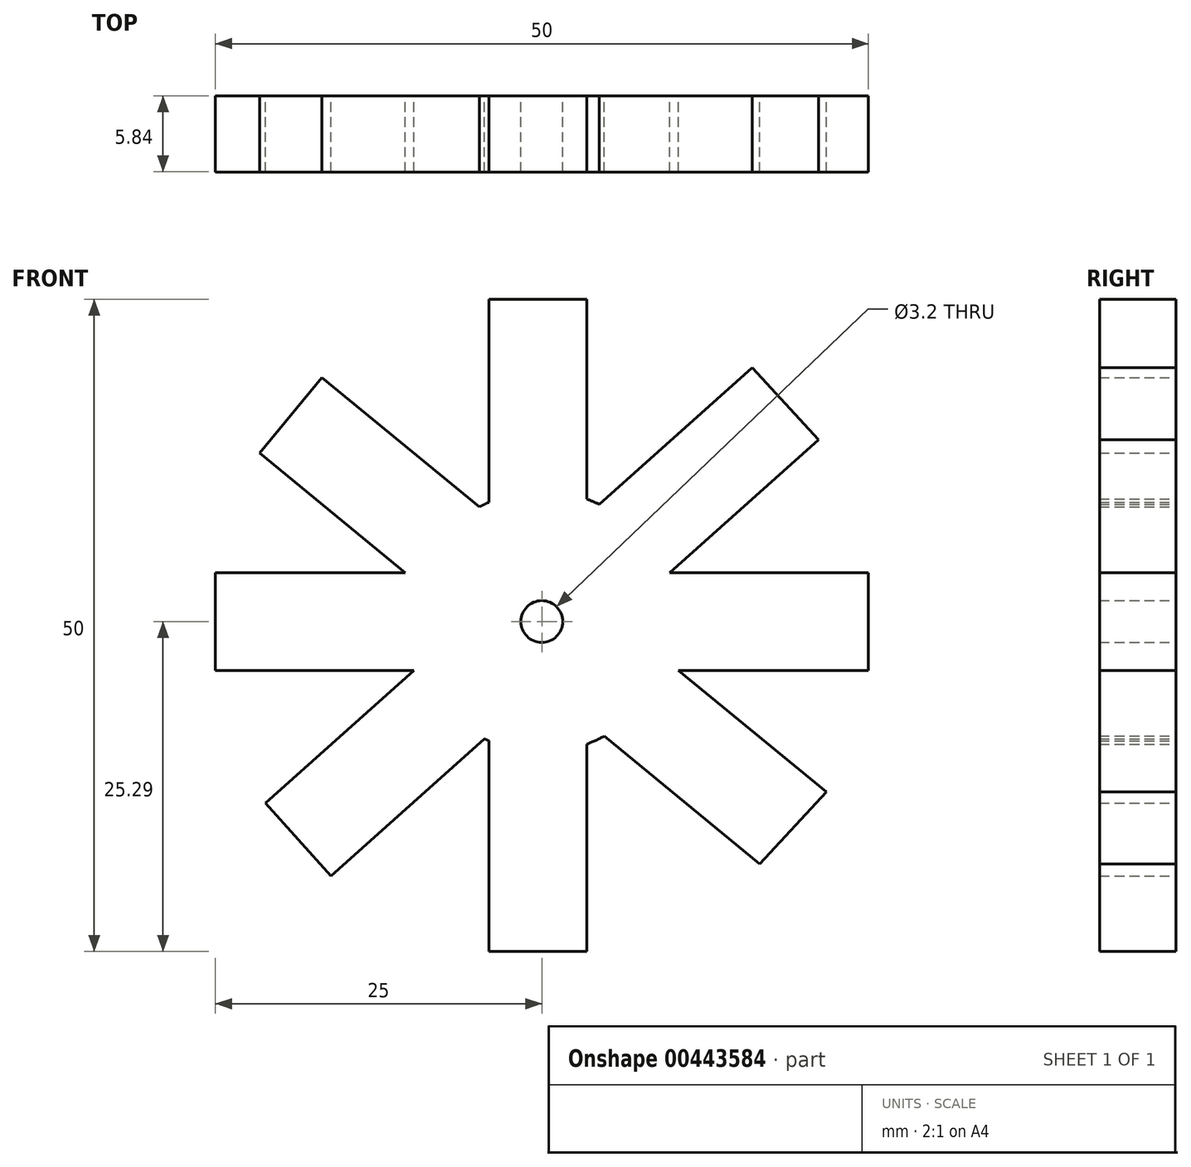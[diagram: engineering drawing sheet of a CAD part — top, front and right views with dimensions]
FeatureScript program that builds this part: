
annotation { "Feature Type Name" : "Feature", "Feature Type Description" : "" }
export const myFeature = defineFeature(function(context is Context, id is Id, definition is map)
    precondition{}
    {
        {
            var Q0;
            Q0=qCreatedBy(makeId("Front.planeOp"),FACE);
            var sketch = newSketch(context, id + "F0", { "sketchPlane" : qUnion([Q0])});
            skCircle(sketch, "E0", {"center": v(0, 0) * mm, "radius": 10 * mm});
            skCircle(sketch, "E1", {"center": v(0, 0) * mm, "radius": 1.6 * mm});
            skLineSegment(sketch, "E2.right", {"start": v(0, 2.75) * mm, "end": v(0, -2.75) * mm});
            skLineSegment(sketch, "E3.bottom", {"start": v(-4.06, 24.71) * mm, "end": v(3.44, 24.71) * mm});
            skLineSegment(sketch, "E3.top", {"start": v(-4.06, -25.29) * mm, "end": v(3.44, -25.29) * mm});
            skLineSegment(sketch, "E3.left", {"start": v(-4.06, 24.71) * mm, "end": v(-4.06, -25.29) * mm});
            skLineSegment(sketch, "E3.right", {"start": v(3.44, 24.71) * mm, "end": v(3.44, -25.29) * mm});
            skLineSegment(sketch, "E4", {"start": v(-21.15, -13.9) * mm, "end": v(16.1, 19.45) * mm});
            skLineSegment(sketch, "E5", {"start": v(-21.15, -13.9) * mm, "end": v(-16.15, -19.5) * mm});
            skLineSegment(sketch, "E6", {"start": v(-16.15, -19.5) * mm, "end": v(21.2, 13.95) * mm});
            skLineSegment(sketch, "E7", {"start": v(16.1, 19.45) * mm, "end": v(21.2, 13.95) * mm});
            skPoint(sketch, "E8", {"position": v(3.44, -0.29) * mm});
            skPoint(sketch, "E9", {"position": v(-0.31, 24.71) * mm});
            skPoint(sketch, "E10", {"position": v(-18.65, -16.7) * mm});
            skPoint(sketch, "E11", {"position": v(18.65, 16.7) * mm});
            skLineSegment(sketch, "E12.bottom", {"start": v(-25, 3.75) * mm, "end": v(25, 3.75) * mm});
            skLineSegment(sketch, "E12.top", {"start": v(-25, -3.75) * mm, "end": v(25, -3.75) * mm});
            skLineSegment(sketch, "E12.left", {"start": v(-25, 3.75) * mm, "end": v(-25, -3.75) * mm});
            skLineSegment(sketch, "E12.right", {"start": v(25, 3.75) * mm, "end": v(25, -3.75) * mm});
            skPoint(sketch, "E13", {"position": v(-25, 0) * mm});
            skPoint(sketch, "E14", {"position": v(25, 0) * mm});
            skLineSegment(sketch, "E15", {"start": v(-21.61, 12.9) * mm, "end": v(16.69, -18.56) * mm});
            skLineSegment(sketch, "E16", {"start": v(-21.61, 12.9) * mm, "end": v(-16.85, 18.7) * mm});
            skLineSegment(sketch, "E17", {"start": v(-16.85, 18.7) * mm, "end": v(21.78, -13.04) * mm});
            skLineSegment(sketch, "E18", {"start": v(16.69, -18.56) * mm, "end": v(21.78, -13.04) * mm});
            skPoint(sketch, "E19", {"position": v(-19.23, 15.8) * mm});
            skPoint(sketch, "E20", {"position": v(19.23, -15.8) * mm});
            skSolve(sketch);
        }
        {
            var Q0;
            Q0 = qSketchRegion(id + "F0", true);
            var Q1;
            {var subQ0=sQuery(id+"F0.wireOp",EDGE,"E12.bottom");var subQ1=sQuery(id+"F0.wireOp",EDGE,"E3.left");var subQ2=makeQuery(id+"F0.imprint","INTERSECT",VERTEX,{"derivedFrom":[subQ1,subQ0]});Q1=makeQuery(id+"F0.imprint","IMPRINT",FACE,{"disambiguationData":[TD([[makeQuery(id+"F0.imprint","IMPRINT",EDGE,{"disambiguationData":[TD([[subQ2,-1.0]])],"derivedFrom":subQ1}),-1.0]])]});}
            var Q2;
            {var subQ0=sQuery(id+"F0.wireOp",EDGE,"E15");var subQ1=sQuery(id+"F0.wireOp",EDGE,"E3.left");var subQ2=makeQuery(id+"F0.imprint","INTERSECT",VERTEX,{"derivedFrom":[subQ1,subQ0]});Q2=makeQuery(id+"F0.imprint","IMPRINT",FACE,{"disambiguationData":[TD([[makeQuery(id+"F0.imprint","IMPRINT",EDGE,{"disambiguationData":[TD([[subQ2,-1.0]])],"derivedFrom":subQ1}),-1.0]])]});}
            var Q3;
            {var subQ0=sQuery(id+"F0.wireOp",EDGE,"E17");var subQ1=sQuery(id+"F0.wireOp",EDGE,"E3.left");var subQ2=makeQuery(id+"F0.imprint","INTERSECT",VERTEX,{"derivedFrom":[subQ1,subQ0]});Q3=makeQuery(id+"F0.imprint","IMPRINT",FACE,{"disambiguationData":[TD([[makeQuery(id+"F0.imprint","IMPRINT",EDGE,{"disambiguationData":[TD([[subQ2,-1.0]])],"derivedFrom":subQ1}),1.0]])]});}
            var Q4;
            {var subQ0=sQuery(id+"F0.wireOp",EDGE,"E4");var subQ1=sQuery(id+"F0.wireOp",EDGE,"E3.right");var subQ2=makeQuery(id+"F0.imprint","INTERSECT",VERTEX,{"derivedFrom":[subQ1,subQ0]});Q4=makeQuery(id+"F0.imprint","IMPRINT",FACE,{"disambiguationData":[TD([[makeQuery(id+"F0.imprint","IMPRINT",EDGE,{"disambiguationData":[TD([[subQ2,-1.0]])],"derivedFrom":subQ1}),-1.0]])]});}
            var Q5;
            {var subQ0=sQuery(id+"F0.wireOp",EDGE,"E12.bottom");var subQ1=sQuery(id+"F0.wireOp",EDGE,"E4");var subQ2=makeQuery(id+"F0.imprint","INTERSECT",VERTEX,{"derivedFrom":[subQ1,subQ0]});Q5=makeQuery(id+"F0.imprint","IMPRINT",FACE,{"disambiguationData":[TD([[makeQuery(id+"F0.imprint","IMPRINT",EDGE,{"disambiguationData":[TD([[subQ2,-1.0]])],"derivedFrom":subQ1}),-1.0]])]});}
            var Q6;
            {var subQ0=sQuery(id+"F0.wireOp",EDGE,"E17");var subQ1=sQuery(id+"F0.wireOp",EDGE,"E3.right");var subQ2=makeQuery(id+"F0.imprint","INTERSECT",VERTEX,{"derivedFrom":[subQ1,subQ0]});Q6=makeQuery(id+"F0.imprint","IMPRINT",FACE,{"disambiguationData":[TD([[makeQuery(id+"F0.imprint","IMPRINT",EDGE,{"disambiguationData":[TD([[subQ2,-1.0]])],"derivedFrom":subQ1}),1.0]])]});}
            var Q7;
            {var subQ0=sQuery(id+"F0.wireOp",EDGE,"E4");var subQ1=sQuery(id+"F0.wireOp",EDGE,"E3.left");var subQ2=makeQuery(id+"F0.imprint","INTERSECT",VERTEX,{"derivedFrom":[subQ1,subQ0]});Q7=makeQuery(id+"F0.imprint","IMPRINT",FACE,{"disambiguationData":[TD([[makeQuery(id+"F0.imprint","IMPRINT",EDGE,{"disambiguationData":[TD([[subQ2,-1.0]])],"derivedFrom":subQ1}),-1.0]])]});}
            var Q8;
            {var subQ0=sQuery(id+"F0.wireOp",EDGE,"E12.top");var subQ1=sQuery(id+"F0.wireOp",EDGE,"E3.right");var subQ2=makeQuery(id+"F0.imprint","INTERSECT",VERTEX,{"derivedFrom":[subQ1,subQ0]});Q8=makeQuery(id+"F0.imprint","IMPRINT",FACE,{"disambiguationData":[TD([[makeQuery(id+"F0.imprint","IMPRINT",EDGE,{"disambiguationData":[TD([[subQ2,-1.0]])],"derivedFrom":subQ1}),-1.0]])]});}
            var Q9;
            {var subQ0=sQuery(id+"F0.wireOp",EDGE,"E15");var subQ1=sQuery(id+"F0.wireOp",EDGE,"E6");var subQ2=makeQuery(id+"F0.imprint","INTERSECT",VERTEX,{"derivedFrom":[subQ1,subQ0]});Q9=makeQuery(id+"F0.imprint","IMPRINT",FACE,{"disambiguationData":[TD([[makeQuery(id+"F0.imprint","IMPRINT",EDGE,{"disambiguationData":[TD([[subQ2,-1.0]])],"derivedFrom":subQ1}),1.0]])]});}
            var Q10;
            {var subQ0=sQuery(id+"F0.wireOp",EDGE,"E12.bottom");var subQ1=sQuery(id+"F0.wireOp",EDGE,"E3.left");var subQ2=makeQuery(id+"F0.imprint","INTERSECT",VERTEX,{"derivedFrom":[subQ1,subQ0]});Q10=makeQuery(id+"F0.imprint","IMPRINT",FACE,{"disambiguationData":[TD([[makeQuery(id+"F0.imprint","IMPRINT",EDGE,{"disambiguationData":[TD([[subQ2,-1.0]])],"derivedFrom":subQ1}),1.0]])]});}
            var Q11;
            {var subQ5=sQuery(id+"F0.wireOp",EDGE,"E2.right");var subQ6=sQuery(id+"F0.wireOp",EDGE,"E1");var subQ7=makeQuery(id+"F0.imprint","INTERSECT",VERTEX,{"disambiguationData":[OD(0.0)],"derivedFrom":[subQ6,subQ5]});Q11=makeQuery(id+"F0.imprint","IMPRINT",FACE,{"disambiguationData":[TD([[makeQuery(id+"F0.imprint","IMPRINT",EDGE,{"disambiguationData":[TD([[subQ7,-1.0]])],"derivedFrom":subQ6}),-1.0]])]});}
            var Q12;
            {var subQ0=sQuery(id+"F0.wireOp",EDGE,"E12.top");var subQ1=sQuery(id+"F0.wireOp",EDGE,"E3.left");var subQ2=makeQuery(id+"F0.imprint","INTERSECT",VERTEX,{"derivedFrom":[subQ1,subQ0]});Q12=makeQuery(id+"F0.imprint","IMPRINT",FACE,{"disambiguationData":[TD([[makeQuery(id+"F0.imprint","IMPRINT",EDGE,{"disambiguationData":[TD([[subQ2,-1.0]])],"derivedFrom":subQ1}),1.0]])]});}
            var Q13;
            {var subQ0=sQuery(id+"F0.wireOp",EDGE,"E15");var subQ1=sQuery(id+"F0.wireOp",EDGE,"E3.left");var subQ2=makeQuery(id+"F0.imprint","INTERSECT",VERTEX,{"derivedFrom":[subQ1,subQ0]});Q13=makeQuery(id+"F0.imprint","IMPRINT",FACE,{"disambiguationData":[TD([[makeQuery(id+"F0.imprint","IMPRINT",EDGE,{"disambiguationData":[TD([[subQ2,-1.0]])],"derivedFrom":subQ1}),1.0]])]});}
            var Q14;
            {var subQ0=sQuery(id+"F0.wireOp",EDGE,"E12.bottom");var subQ1=sQuery(id+"F0.wireOp",EDGE,"E3.right");var subQ2=makeQuery(id+"F0.imprint","INTERSECT",VERTEX,{"derivedFrom":[subQ1,subQ0]});Q14=makeQuery(id+"F0.imprint","IMPRINT",FACE,{"disambiguationData":[TD([[makeQuery(id+"F0.imprint","IMPRINT",EDGE,{"disambiguationData":[TD([[subQ2,-1.0]])],"derivedFrom":subQ1}),1.0]])]});}
            var Q15;
            {var subQ6=sQuery(id+"F0.wireOp",EDGE,"E2.right");var subQ8=sQuery(id+"F0.wireOp",EDGE,"E1");var subQ13=makeQuery(id+"F0.imprint","INTERSECT",VERTEX,{"disambiguationData":[OD(0.0)],"derivedFrom":[subQ8,subQ6]});Q15=makeQuery(id+"F0.imprint","IMPRINT",FACE,{"disambiguationData":[TD([[makeQuery(id+"F0.imprint","IMPRINT",EDGE,{"disambiguationData":[TD([[subQ13,1.0]])],"derivedFrom":subQ8}),-1.0]])]});}
            var Q16;
            {var subQ0=sQuery(id+"F0.wireOp",EDGE,"E6");var subQ1=sQuery(id+"F0.wireOp",EDGE,"E3.right");var subQ2=makeQuery(id+"F0.imprint","INTERSECT",VERTEX,{"derivedFrom":[subQ1,subQ0]});Q16=makeQuery(id+"F0.imprint","IMPRINT",FACE,{"disambiguationData":[TD([[makeQuery(id+"F0.imprint","IMPRINT",EDGE,{"disambiguationData":[TD([[subQ2,-1.0]])],"derivedFrom":subQ1}),-1.0]])]});}
            var Q17;
            {var subQ0=sQuery(id+"F0.wireOp",EDGE,"E12.bottom");var subQ1=sQuery(id+"F0.wireOp",EDGE,"E3.right");var subQ2=makeQuery(id+"F0.imprint","INTERSECT",VERTEX,{"derivedFrom":[subQ1,subQ0]});Q17=makeQuery(id+"F0.imprint","IMPRINT",FACE,{"disambiguationData":[TD([[makeQuery(id+"F0.imprint","IMPRINT",EDGE,{"disambiguationData":[TD([[subQ2,-1.0]])],"derivedFrom":subQ1}),-1.0]])]});}
            var Q18;
            {var subQ0=sQuery(id+"F0.wireOp",EDGE,"E6");var subQ1=sQuery(id+"F0.wireOp",EDGE,"E3.right");var subQ2=makeQuery(id+"F0.imprint","INTERSECT",VERTEX,{"derivedFrom":[subQ1,subQ0]});Q18=makeQuery(id+"F0.imprint","IMPRINT",FACE,{"disambiguationData":[TD([[makeQuery(id+"F0.imprint","IMPRINT",EDGE,{"disambiguationData":[TD([[subQ2,-1.0]])],"derivedFrom":subQ1}),1.0]])]});}
            var Q19;
            {var subQ0=sQuery(id+"F0.wireOp",EDGE,"E15");var subQ1=sQuery(id+"F0.wireOp",EDGE,"E0");var subQ2=makeQuery(id+"F0.imprint","INTERSECT",VERTEX,{"disambiguationData":[OD(1.0)],"derivedFrom":[subQ1,subQ0]});Q19=makeQuery(id+"F0.imprint","IMPRINT",FACE,{"disambiguationData":[TD([[makeQuery(id+"F0.imprint","IMPRINT",EDGE,{"disambiguationData":[TD([[subQ2,-1.0]])],"derivedFrom":subQ1}),1.0]])]});}
            var Q20;
            {var subQ0=sQuery(id+"F0.wireOp",EDGE,"E6");var subQ1=sQuery(id+"F0.wireOp",EDGE,"E0");var subQ2=makeQuery(id+"F0.imprint","INTERSECT",VERTEX,{"disambiguationData":[OD(1.0)],"derivedFrom":[subQ1,subQ0]});Q20=makeQuery(id+"F0.imprint","IMPRINT",FACE,{"disambiguationData":[TD([[makeQuery(id+"F0.imprint","IMPRINT",EDGE,{"disambiguationData":[TD([[subQ2,1.0]])],"derivedFrom":subQ1}),1.0]])]});}
            extrude(context, id + "F1", {"entities" : qUnion([Q0, Q1, Q2, Q3, Q4, Q5, Q6, Q7, Q8, Q9, Q10, Q11, Q12, Q13, Q14, Q15, Q16, Q17, Q18, Q19, Q20]), "depth" : 5.84 * mm});
        }
    });
